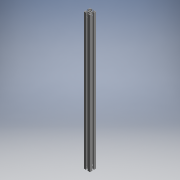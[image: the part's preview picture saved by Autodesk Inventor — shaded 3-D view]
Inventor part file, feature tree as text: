
AUTODESK INVENTOR PART (.ipt)
format: ipt  version: 2017.3 (Build 213256000, 256)  size: 300,544 bytes
history: native  units: mm (DEFAULTED — no unit token found)
features: other x7, sketch x4, revolve x2, extrude x1, hole x1
ambient origin geometry x8: Origin, YZ Plane, XZ Plane, XY Plane, X Axis, Y Axis, Z Axis, Center Point
bodies: Solid1 (feature_tree)
feature tree (15):
  extrude  "Extrusion1"  TaperAngle=360.0deg  [1 undecoded]
  hole  "Hole1"  [1 undecoded]
  revolve  "Revolution1"  [1 undecoded]
  revolve  "Revolution2"  [1 undecoded]
  other  "C1_XY"
  other  "C1_YZ"
  other  "C1_ZX"
  other  "C1_X"
  other  "C1_Y"
  other  "C1_Z"
  other  "C1_Center"
  sketch  "Sketch_75"
  sketch  "Sketch2"  dims[d0=437.0mm d1=0.0mm]
  sketch  "Sketch_30"  dims[d2=4.2mm d3=6.0mm d4=4.0mm d5=2.0mm d6=90.0deg d7=437.0mm d8=0.0mm d9=360.0deg]
  sketch  "Sketch_31"  dims[d10=360.0deg d11=0.0mm]
note: 4 required parameter values undecoded (feature->parameter linkage not recoverable at this tier; creation-order binding heuristic only, values carry confidence <= 0.55)
